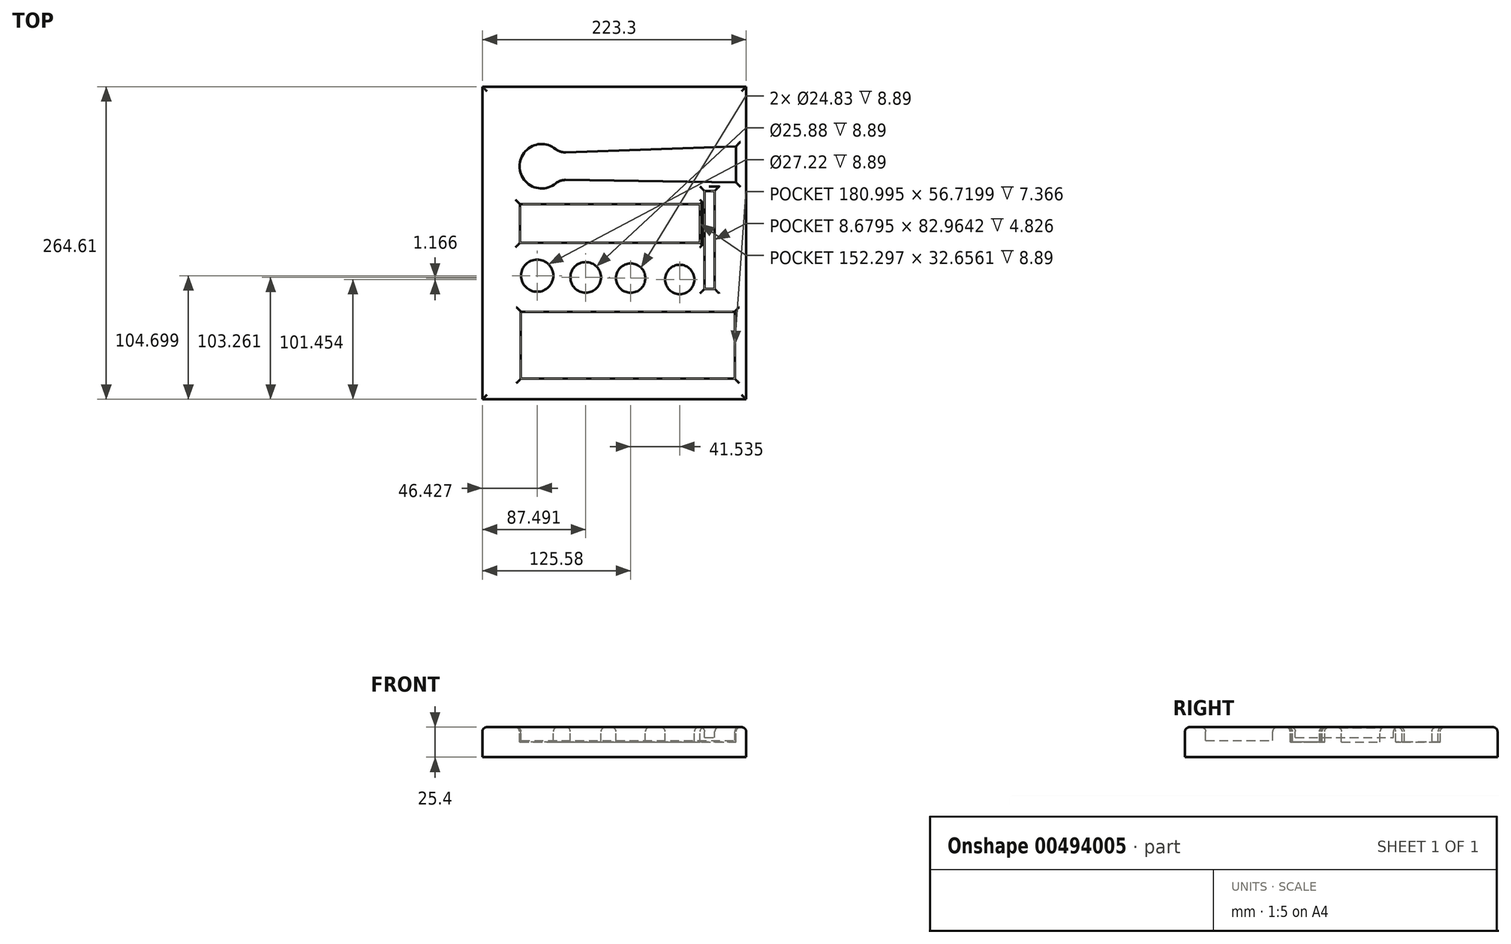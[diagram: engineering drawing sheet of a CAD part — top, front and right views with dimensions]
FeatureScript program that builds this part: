
annotation { "Feature Type Name" : "Feature", "Feature Type Description" : "" }
export const myFeature = defineFeature(function(context is Context, id is Id, definition is map)
    precondition{}
    {
        {
            var Q0;
            Q0=qCreatedBy(makeId("Top.planeOp"),FACE);
            var sketch = newSketch(context, id + "F0", { "sketchPlane" : qUnion([Q0])});
            skLineSegment(sketch, "E0.bottom", {"start": v(0, 0) * mm, "end": v(-223.3, 0) * mm});
            skLineSegment(sketch, "E0.top", {"start": v(0, 264.6) * mm, "end": v(-223.3, 264.6) * mm});
            skLineSegment(sketch, "E0.left", {"start": v(0, 0) * mm, "end": v(0, 264.6) * mm});
            skLineSegment(sketch, "E0.right", {"start": v(-223.3, 0) * mm, "end": v(-223.3, 264.6) * mm});
            skSolve(sketch);
        }
        {
            var Q0;
            Q0=makeQuery(id+"F0.imprint","IMPRINT",FACE,{"disambiguationData":[TD([[makeQuery(id+"F0.imprint","IMPRINT",EDGE,{"derivedFrom":sQuery(id+"F0.wireOp",EDGE,"E0.bottom")}),-1.0]])]});
            extrude(context, id + "F1", {"entities" : qUnion([Q0]), "depth" : 25.4 * mm});
        }
        {
            var Q0;
            Q0=makeQuery(id+"F1.opExtrude","CAP_FACE",FACE,{"disambiguationData":[OSD([sQuery(id+"F0.wireOp",EDGE,"E0.bottom"),sQuery(id+"F0.wireOp",EDGE,"E0.top"),sQuery(id+"F0.wireOp",EDGE,"E0.left"),sQuery(id+"F0.wireOp",EDGE,"E0.right")])],"isStart":false});
            var sketch = newSketch(context, id + "F2", { "sketchPlane" : qUnion([Q0])});
            skLineSegment(sketch, "E1.bottom", {"start": v(-190.67, 17.53) * mm, "end": v(-9.67, 17.53) * mm});
            skLineSegment(sketch, "E1.top", {"start": v(-190.67, 74.24) * mm, "end": v(-9.67, 74.24) * mm});
            skLineSegment(sketch, "E1.left", {"start": v(-190.67, 17.53) * mm, "end": v(-190.67, 74.24) * mm});
            skLineSegment(sketch, "E1.right", {"start": v(-9.67, 17.53) * mm, "end": v(-9.67, 74.24) * mm});
            skSolve(sketch);
        }
        {
            var Q0;
            Q0=makeQuery(id+"F2.imprint","IMPRINT",FACE,{"disambiguationData":[TD([[makeQuery(id+"F2.imprint","IMPRINT",EDGE,{"derivedFrom":sQuery(id+"F2.wireOp",EDGE,"E1.bottom")}),1.0]])]});
            extrude(context, id + "F3", {"entities" : qUnion([Q0]), "operationType" : NewBodyOperationType.REMOVE, "oppositeDirection" : true, "depth" : 11.18 * mm});
        }
        {
            var Q0;
            Q0=makeQuery(id+"F1.opExtrude","CAP_FACE",FACE,{"disambiguationData":[OSD([sQuery(id+"F0.wireOp",EDGE,"E0.bottom"),sQuery(id+"F0.wireOp",EDGE,"E0.top"),sQuery(id+"F0.wireOp",EDGE,"E0.left"),sQuery(id+"F0.wireOp",EDGE,"E0.right")])],"isStart":false});
            var sketch = newSketch(context, id + "F4", { "sketchPlane" : qUnion([Q0])});
            skCircle(sketch, "E2", {"center": v(-176.87, 104.7) * mm, "radius": 13.61 * mm});
            skCircle(sketch, "E3", {"center": v(-135.8, 103.26) * mm, "radius": 12.94 * mm});
            skCircle(sketch, "E4", {"center": v(-97.72, 102.62) * mm, "radius": 12.41 * mm});
            skCircle(sketch, "E5", {"center": v(-56.18, 101.45) * mm, "radius": 12.41 * mm});
            skSolve(sketch);
        }
        {
            var Q0;
            Q0=makeQuery(id+"F4.imprint","IMPRINT",FACE,{"disambiguationData":[TD([[makeQuery(id+"F4.imprint","IMPRINT",EDGE,{"derivedFrom":sQuery(id+"F4.wireOp",EDGE,"E2")}),1.0]])]});
            var Q1;
            Q1=makeQuery(id+"F4.imprint","IMPRINT",FACE,{"disambiguationData":[TD([[makeQuery(id+"F4.imprint","IMPRINT",EDGE,{"derivedFrom":sQuery(id+"F4.wireOp",EDGE,"E3")}),1.0]])]});
            var Q2;
            Q2=makeQuery(id+"F4.imprint","IMPRINT",FACE,{"disambiguationData":[TD([[makeQuery(id+"F4.imprint","IMPRINT",EDGE,{"derivedFrom":sQuery(id+"F4.wireOp",EDGE,"E4")}),1.0]])]});
            var Q3;
            Q3=makeQuery(id+"F4.imprint","IMPRINT",FACE,{"disambiguationData":[TD([[makeQuery(id+"F4.imprint","IMPRINT",EDGE,{"derivedFrom":sQuery(id+"F4.wireOp",EDGE,"E5")}),1.0]])]});
            extrude(context, id + "F5", {"entities" : qUnion([Q0, Q1, Q2, Q3]), "operationType" : NewBodyOperationType.REMOVE, "oppositeDirection" : true, "depth" : 12.7 * mm});
        }
        {
            var Q0;
            Q0=makeQuery(id+"F1.opExtrude","CAP_FACE",FACE,{"disambiguationData":[OSD([sQuery(id+"F0.wireOp",EDGE,"E0.bottom"),sQuery(id+"F0.wireOp",EDGE,"E0.top"),sQuery(id+"F0.wireOp",EDGE,"E0.left"),sQuery(id+"F0.wireOp",EDGE,"E0.right")])],"isStart":false});
            var sketch = newSketch(context, id + "F6", { "sketchPlane" : qUnion([Q0])});
            skSolve(sketch);
        }
        {
            var Q0;
            Q0=makeQuery(id+"F6.imprint","IMPRINT",FACE,{"disambiguationData":[TD([[makeQuery(id+"F6.imprint","IMPRINT",EDGE,{"derivedFrom":makeQuery(id+"F1.opExtrude","CAP_EDGE",EDGE,{"disambiguationData":[OSD([sQuery(id+"F0.wireOp",EDGE,"E0.bottom")])],"isStart":false})}),-1.0]])]});
            var sketch = newSketch(context, id + "F7", { "sketchPlane" : qUnion([Q0])});
            skLineSegment(sketch, "E6.bottom", {"start": v(-35.22, 93.44) * mm, "end": v(-26.54, 93.44) * mm});
            skLineSegment(sketch, "E6.top", {"start": v(-35.22, 176.4) * mm, "end": v(-26.54, 176.4) * mm});
            skLineSegment(sketch, "E6.left", {"start": v(-35.22, 93.44) * mm, "end": v(-35.22, 176.4) * mm});
            skLineSegment(sketch, "E6.right", {"start": v(-26.54, 93.44) * mm, "end": v(-26.54, 176.4) * mm});
            skSolve(sketch);
        }
        {
            var Q0;
            Q0=makeQuery(id+"F7.imprint","IMPRINT",FACE,{"disambiguationData":[TD([[makeQuery(id+"F7.imprint","IMPRINT",EDGE,{"derivedFrom":sQuery(id+"F7.wireOp",EDGE,"E6.bottom")}),1.0]])]});
            extrude(context, id + "F8", {"entities" : qUnion([Q0]), "operationType" : NewBodyOperationType.REMOVE, "oppositeDirection" : true, "depth" : 8.64 * mm});
        }
        {
            var Q0;
            Q0=makeQuery(id+"F6.imprint","IMPRINT",FACE,{"disambiguationData":[TD([[makeQuery(id+"F6.imprint","IMPRINT",EDGE,{"derivedFrom":makeQuery(id+"F1.opExtrude","CAP_EDGE",EDGE,{"disambiguationData":[OSD([sQuery(id+"F0.wireOp",EDGE,"E0.bottom")])],"isStart":false})}),-1.0]])]});
            var sketch = newSketch(context, id + "F9", { "sketchPlane" : qUnion([Q0])});
            skLineSegment(sketch, "E7", {"start": v(-8.6, 183.71) * mm, "end": v(-8.6, 214.12) * mm});
            skLineSegment(sketch, "E8.bottom", {"start": v(-191.41, 132.49) * mm, "end": v(-39.11, 132.49) * mm});
            skLineSegment(sketch, "E8.top", {"start": v(-191.41, 165.14) * mm, "end": v(-39.11, 165.14) * mm});
            skLineSegment(sketch, "E8.left", {"start": v(-191.41, 132.49) * mm, "end": v(-191.41, 165.14) * mm});
            skLineSegment(sketch, "E8.right", {"start": v(-39.11, 132.49) * mm, "end": v(-39.11, 165.14) * mm});
            skArc(sketch, "E9", {"start": v(-158.3, 208.86) * mm, "mid": v(-191.88, 197.32) * mm, "end": v(-158.3, 185.78) * mm});
            skLineSegment(sketch, "E10", {"start": v(-8.6, 183.71) * mm, "end": v(-158.3, 185.78) * mm});
            skLineSegment(sketch, "E11", {"start": v(-158.3, 208.86) * mm, "end": v(-8.6, 214.12) * mm});
            skSolve(sketch);
        }
        {
            var Q0;
            Q0=makeQuery(id+"F9.imprint","IMPRINT",FACE,{"disambiguationData":[TD([[makeQuery(id+"F9.imprint","IMPRINT",EDGE,{"derivedFrom":sQuery(id+"F9.wireOp",EDGE,"E7")}),1.0]])]});
            extrude(context, id + "F10", {"entities" : qUnion([Q0]), "operationType" : NewBodyOperationType.REMOVE, "oppositeDirection" : true, "depth" : 12.7 * mm});
        }
        {
            var Q0;
            Q0 = qSketchRegion(id + "F9", true);
            extrude(context, id + "F11", {"entities" : qUnion([Q0]), "operationType" : NewBodyOperationType.REMOVE, "oppositeDirection" : true, "depth" : 12.7 * mm});
        }
        {
            var Q0;
            Q0=makeQuery(id+"F10.boolean.opBoolean","COPY",EDGE,{"derivedFrom":makeQuery(id+"F10.opExtrude","SWEPT_EDGE",EDGE,{"disambiguationData":[OSD([sQuery(id+"F9.wireOp",EDGE,"E9"),sQuery(id+"F9.wireOp",EDGE,"E11")])]})});
            var Q1;
            Q1=makeQuery(id+"F10.boolean.opBoolean","COPY",EDGE,{"derivedFrom":makeQuery(id+"F10.opExtrude","SWEPT_EDGE",EDGE,{"disambiguationData":[OSD([sQuery(id+"F9.wireOp",EDGE,"E9"),sQuery(id+"F9.wireOp",EDGE,"E10")])]})});
            fillet(context, id + "F12", {"entities" : qUnion([Q0, Q1]), "radius" : 12.7 * mm, "tangentPropagation" : true, "allowEdgeOverflow" : false});
        }
        {
            var Q0;
            Q0=makeQuery(id+"F3.boolean.opBoolean","COPY",EDGE,{"derivedFrom":makeQuery(id+"F3.opExtrude","CAP_EDGE",EDGE,{"disambiguationData":[OSD([sQuery(id+"F2.wireOp",EDGE,"E1.top")])],"isStart":true})});
            var Q1;
            Q1=makeQuery(id+"F3.boolean.opBoolean","COPY",EDGE,{"derivedFrom":makeQuery(id+"F3.opExtrude","CAP_EDGE",EDGE,{"disambiguationData":[OSD([sQuery(id+"F2.wireOp",EDGE,"E1.left")])],"isStart":true})});
            var Q2;
            Q2=makeQuery(id+"F3.boolean.opBoolean","COPY",EDGE,{"derivedFrom":makeQuery(id+"F3.opExtrude","CAP_EDGE",EDGE,{"disambiguationData":[OSD([sQuery(id+"F2.wireOp",EDGE,"E1.bottom")])],"isStart":true})});
            var Q3;
            Q3=makeQuery(id+"F3.boolean.opBoolean","COPY",EDGE,{"derivedFrom":makeQuery(id+"F3.opExtrude","CAP_EDGE",EDGE,{"disambiguationData":[OSD([sQuery(id+"F2.wireOp",EDGE,"E1.right")])],"isStart":true})});
            var Q4;
            Q4=makeQuery(id+"F8.boolean.opBoolean","COPY",EDGE,{"derivedFrom":makeQuery(id+"F8.opExtrude","CAP_EDGE",EDGE,{"disambiguationData":[OSD([sQuery(id+"F7.wireOp",EDGE,"E6.right")])],"isStart":true})});
            var Q5;
            Q5=makeQuery(id+"F8.boolean.opBoolean","COPY",EDGE,{"derivedFrom":makeQuery(id+"F8.opExtrude","CAP_EDGE",EDGE,{"disambiguationData":[OSD([sQuery(id+"F7.wireOp",EDGE,"E6.left")])],"isStart":true})});
            var Q6;
            Q6=makeQuery(id+"F8.boolean.opBoolean","COPY",EDGE,{"derivedFrom":makeQuery(id+"F8.opExtrude","CAP_EDGE",EDGE,{"disambiguationData":[OSD([sQuery(id+"F7.wireOp",EDGE,"E6.bottom")])],"isStart":true})});
            var Q7;
            Q7=makeQuery(id+"F8.boolean.opBoolean","COPY",EDGE,{"derivedFrom":makeQuery(id+"F8.opExtrude","CAP_EDGE",EDGE,{"disambiguationData":[OSD([sQuery(id+"F7.wireOp",EDGE,"E6.top")])],"isStart":true})});
            var Q8;
            Q8=makeQuery(id+"F11.boolean.opBoolean","COPY",EDGE,{"derivedFrom":makeQuery(id+"F11.opExtrude","CAP_EDGE",EDGE,{"disambiguationData":[OSD([sQuery(id+"F9.wireOp",EDGE,"E8.top")])],"isStart":true})});
            var Q9;
            Q9=makeQuery(id+"F11.boolean.opBoolean","COPY",EDGE,{"derivedFrom":makeQuery(id+"F11.opExtrude","CAP_EDGE",EDGE,{"disambiguationData":[OSD([sQuery(id+"F9.wireOp",EDGE,"E8.right")])],"isStart":true})});
            var Q10;
            Q10=makeQuery(id+"F11.boolean.opBoolean","COPY",EDGE,{"derivedFrom":makeQuery(id+"F11.opExtrude","CAP_EDGE",EDGE,{"disambiguationData":[OSD([sQuery(id+"F9.wireOp",EDGE,"E8.bottom")])],"isStart":true})});
            var Q11;
            Q11=makeQuery(id+"F5.boolean.opBoolean","COPY",EDGE,{"derivedFrom":makeQuery(id+"F5.opExtrude","CAP_EDGE",EDGE,{"disambiguationData":[OSD([sQuery(id+"F4.wireOp",EDGE,"E5")])],"isStart":true})});
            var Q12;
            Q12=makeQuery(id+"F5.boolean.opBoolean","COPY",EDGE,{"derivedFrom":makeQuery(id+"F5.opExtrude","CAP_EDGE",EDGE,{"disambiguationData":[OSD([sQuery(id+"F4.wireOp",EDGE,"E4")])],"isStart":true})});
            var Q13;
            Q13=makeQuery(id+"F5.boolean.opBoolean","COPY",EDGE,{"derivedFrom":makeQuery(id+"F5.opExtrude","CAP_EDGE",EDGE,{"disambiguationData":[OSD([sQuery(id+"F4.wireOp",EDGE,"E3")])],"isStart":true})});
            var Q14;
            Q14=makeQuery(id+"F5.boolean.opBoolean","COPY",EDGE,{"derivedFrom":makeQuery(id+"F5.opExtrude","CAP_EDGE",EDGE,{"disambiguationData":[OSD([sQuery(id+"F4.wireOp",EDGE,"E2")])],"isStart":true})});
            var Q15;
            Q15=makeQuery(id+"F10.boolean.opBoolean","COPY",EDGE,{"derivedFrom":makeQuery(id+"F10.opExtrude","CAP_EDGE",EDGE,{"disambiguationData":[OSD([sQuery(id+"F9.wireOp",EDGE,"E11")])],"isStart":true})});
            var Q16;
            Q16=makeQuery(id+"F12.opFillet","BLEND_EDGE",EDGE,{"blendedFrom":[makeQuery(id+"F10.boolean.opBoolean","COPY",EDGE,{"derivedFrom":makeQuery(id+"F10.opExtrude","SWEPT_EDGE",EDGE,{"disambiguationData":[OSD([sQuery(id+"F9.wireOp",EDGE,"E9"),sQuery(id+"F9.wireOp",EDGE,"E11")])]})}),makeQuery(id+"F1.opExtrude","CAP_FACE",FACE,{"disambiguationData":[OSD([sQuery(id+"F0.wireOp",EDGE,"E0.bottom"),sQuery(id+"F0.wireOp",EDGE,"E0.top"),sQuery(id+"F0.wireOp",EDGE,"E0.left"),sQuery(id+"F0.wireOp",EDGE,"E0.right")])],"isStart":false})],"blendedInto":[makeQuery(id+"F1.opExtrude","CAP_FACE",FACE,{"disambiguationData":[OSD([sQuery(id+"F0.wireOp",EDGE,"E0.bottom"),sQuery(id+"F0.wireOp",EDGE,"E0.top"),sQuery(id+"F0.wireOp",EDGE,"E0.left"),sQuery(id+"F0.wireOp",EDGE,"E0.right")])],"isStart":false})]});
            var Q17;
            Q17=makeQuery(id+"F10.boolean.opBoolean","COPY",EDGE,{"derivedFrom":makeQuery(id+"F10.opExtrude","CAP_EDGE",EDGE,{"disambiguationData":[OSD([sQuery(id+"F9.wireOp",EDGE,"E7")])],"isStart":true})});
            var Q18;
            Q18=makeQuery(id+"F1.opExtrude","CAP_FACE",FACE,{"disambiguationData":[OSD([sQuery(id+"F0.wireOp",EDGE,"E0.bottom"),sQuery(id+"F0.wireOp",EDGE,"E0.top"),sQuery(id+"F0.wireOp",EDGE,"E0.left"),sQuery(id+"F0.wireOp",EDGE,"E0.right")])],"isStart":false});
            fillet(context, id + "F13", {"entities" : qUnion([Q0, Q1, Q2, Q3, Q4, Q5, Q6, Q7, Q8, Q9, Q10, Q11, Q12, Q13, Q14, Q15, Q16, Q17, Q18]), "radius" : 3.8 * mm, "tangentPropagation" : true, "allowEdgeOverflow" : false});
        }
    });
